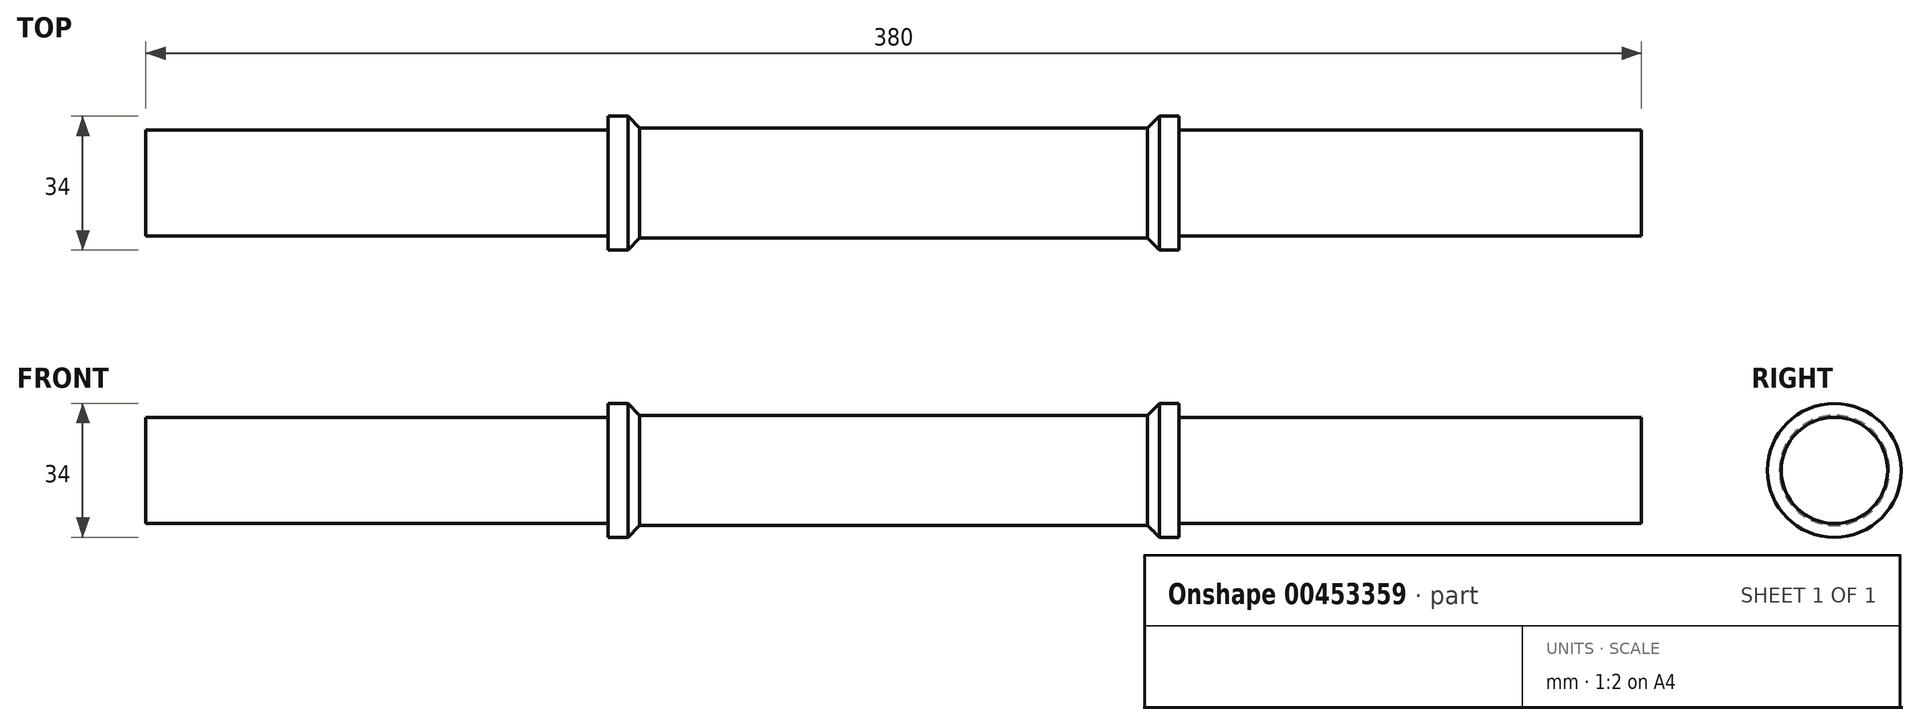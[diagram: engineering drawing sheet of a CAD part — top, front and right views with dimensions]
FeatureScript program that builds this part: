
annotation { "Feature Type Name" : "Feature", "Feature Type Description" : "" }
export const myFeature = defineFeature(function(context is Context, id is Id, definition is map)
    precondition{}
    {
        {
            var Q0;
            Q0=qCreatedBy(makeId("Right.planeOp"),FACE);
            var sketch = newSketch(context, id + "F0", { "sketchPlane" : qUnion([Q0])});
            skCircle(sketch, "E0", {"center": v(0, 0) * mm, "radius": 13.5 * mm});
            skSolve(sketch);
        }
        {
            var Q0;
            Q0 = qSketchRegion(id + "F0", true);
            extrude(context, id + "F1", {"entities" : qUnion([Q0]), "endBound" : BoundingType.SYMMETRIC, "depth" : 380 * mm});
        }
        {
            var Q0;
            Q0=qCreatedBy(makeId("Right.planeOp"),FACE);
            var sketch = newSketch(context, id + "F2", { "sketchPlane" : qUnion([Q0])});
            skCircle(sketch, "E1", {"center": v(0, 0) * mm, "radius": 17 * mm});
            skSolve(sketch);
        }
        {
            var Q0;
            Q0 = qSketchRegion(id + "F2", true);
            extrude(context, id + "F3", {"entities" : qUnion([Q0]), "operationType" : NewBodyOperationType.ADD, "endBound" : BoundingType.SYMMETRIC, "depth" : 145 * mm});
        }
        {
            var Q0;
            Q0=qCreatedBy(makeId("Right.planeOp"),FACE);
            var sketch = newSketch(context, id + "F4", { "sketchPlane" : qUnion([Q0])});
            skCircle(sketch, "E2", {"center": v(0, 0) * mm, "radius": 14 * mm});
            skCircle(sketch, "E3", {"center": v(0, 0) * mm, "radius": 17.5 * mm});
            skSolve(sketch);
        }
        {
            var Q0;
            Q0 = qSketchRegion(id + "F4", true);
            extrude(context, id + "F5", {"entities" : qUnion([Q0]), "operationType" : NewBodyOperationType.REMOVE, "endBound" : BoundingType.SYMMETRIC, "depth" : 135 * mm});
        }
        {
            var Q0;
            Q0=makeQuery(id+"F5.boolean.opBoolean","COPY",EDGE,{"derivedFrom":makeQuery(id+"F5.opExtrude","CAP_EDGE",EDGE,{"disambiguationData":[OSD([sQuery(id+"F4.wireOp",EDGE,"E2")])],"isStart":true})});
            var Q1;
            Q1=makeQuery(id+"F5.boolean.opBoolean","COPY",EDGE,{"derivedFrom":makeQuery(id+"F5.opExtrude","CAP_EDGE",EDGE,{"disambiguationData":[OSD([sQuery(id+"F4.wireOp",EDGE,"E2")])],"isStart":false})});
            chamfer(context, id + "F6", {"entities" : qUnion([Q0, Q1]), "width" : 3 * mm, "tangentPropagation" : true});
        }
    });
